# Revit family: P190780JX-131c_JED3536GS_Black-StainlessSteelTrim_JA_Cooking_Cooktops
name_source: partatom
category: Specialty Equipment
units: mm (PartAtom-declared; Revit-internal decimal feet)

## family parameters
Always vertical = Yes
Cut with Voids When Loaded = No
Enable Cutting in Views = No
Maintain Annotation Orientation = No
Part Type = Normal
Room Calculation Point = No
Round Connector Dimension = Use Diameter
Shared = No
Work Plane-Based = No

## types (1)
- JED3536GS
    Amps = 0 A
    Body Material = ARCAT - Metal - Steel - Stainless
    Cooktop Material = ARCAT - Glass - Tempered - Black
    Default Elevation = 0"
    Depth = 22 1/16"
    Description = Euro-Style 36" JX3™ Electric Downdraft Cooktop
Table de cuisson électrique Jenn-Air® JX3® à évacuation descendante, 36 po
    Dimension Guide = http://access.whirlpool.com Guide&sku=JED3536GS&language=EN
http://access.whirlpool.com Guide&sku=JED3536GS&language=EN
    Family Name = RADIANT & INDUCTION DOWNDRAFT COOKTOP - 36"
    Feature 1 = JX3™ Downdraft Ventilation System with 3 Speeds
Ventilation à évacuation descendante JX3™ à 3 vitesses
    Feature 2 = Perimetric Extraction
Extraction périmétrique
    Feature 3 = 12"/9"/6" Triple-Choice™ Element
Élément Triple-Choice™ de 12 po/ 9 po/ 6 po
    Height = 3 21/32"
    Installation-Fabrication = http://access.whirlpool.com Instruction&sku=JED3536GS&language=EN
http://access.whirlpool.com Instruction&sku=JED3536GS&language=FR
    Knob Material = ARCAT - Metal - Steel - Gray
    Manufacturer = Jenn Air
    Model = JED3536GS
    Voltage = 0 V
    Width = 36 5/16"

## geometry (parser evidence)
native form markers: Sweep x3
no freeform markers — native parametric forms only
